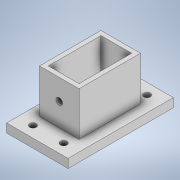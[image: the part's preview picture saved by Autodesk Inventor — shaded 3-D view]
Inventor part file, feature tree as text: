
AUTODESK INVENTOR PART (.ipt)
format: ipt  version: 2022 (Build 260153000, 153)  size: 147,456 bytes
history: native  units: mm
features: extrude x4, sketch x4
ambient origin geometry x8: Origin, YZ Plane, XZ Plane, XY Plane, X Axis, Y Axis, Z Axis, Center Point
bodies: Solid1 (feature_tree)
feature tree (8):
  extrude  "Extrusion1"  Depth=12.0mm
  extrude  "Extrusion3"  Depth=1.0mm
  extrude  "Extrusion5"  Depth=1.75mm
  extrude  "Extrusion6"  Depth=5.0mm TaperAngle=0.0deg
  sketch  "Sketch1"  dims[d0=7.0mm d1=12.0mm]
  sketch  "Sketch3"  dims[d3=1.0mm d4=0.0mm d8=0.75mm]
  sketch  "Sketch7"  dims[d9=1.25mm d10=1.75mm]
  sketch  "Sketch8"  dims[d11=20.0mm d13=3.5mm d14=20.0mm d16=9.5mm d19=5.0mm d20=0.0mm d28=1.75mm d29=1.75mm d30=3.0mm d31=3.0mm d32=0.5mm d33=5.0mm d34=0.0mm d35=0.75mm d36=2.0mm d37=2.25mm d38=0.0mm d39=0.0mm d21=0.5mm d22=0.872665mm d23=0.5mm d24=0.872665mm]
